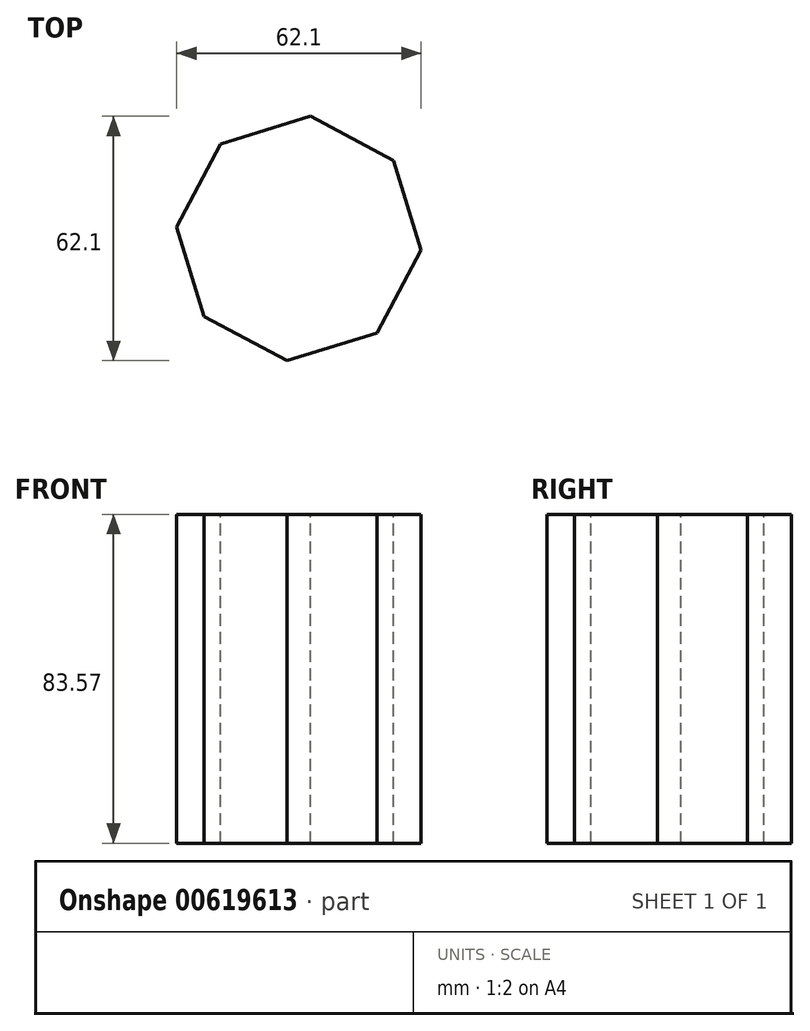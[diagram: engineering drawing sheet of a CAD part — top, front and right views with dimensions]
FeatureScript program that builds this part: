
annotation { "Feature Type Name" : "Feature", "Feature Type Description" : "" }
export const myFeature = defineFeature(function(context is Context, id is Id, definition is map)
    precondition{}
    {
        {
            var Q0;
            Q0=qCreatedBy(makeId("Top.planeOp"),FACE);
            var sketch = newSketch(context, id + "F0", { "sketchPlane" : qUnion([Q0])});
            skCircle(sketch, "E0.cCircle", {"center": v(0, 0) * mm, "radius": 28.82 * mm, "construction": true});
            skLineSegment(sketch, "E0.0", {"start": v(-19.86, 24.06) * mm, "end": v(2.97, 31.05) * mm});
            skLineSegment(sketch, "E0.1", {"start": v(2.97, 31.05) * mm, "end": v(24.06, 19.86) * mm});
            skLineSegment(sketch, "E0.2", {"start": v(24.06, 19.86) * mm, "end": v(31.05, -2.97) * mm});
            skLineSegment(sketch, "E0.3", {"start": v(31.05, -2.97) * mm, "end": v(19.86, -24.06) * mm});
            skLineSegment(sketch, "E0.4", {"start": v(19.86, -24.06) * mm, "end": v(-2.97, -31.05) * mm});
            skLineSegment(sketch, "E0.5", {"start": v(-2.97, -31.05) * mm, "end": v(-24.06, -19.86) * mm});
            skLineSegment(sketch, "E0.6", {"start": v(-24.06, -19.86) * mm, "end": v(-31.05, 2.97) * mm});
            skLineSegment(sketch, "E0.7", {"start": v(-31.05, 2.97) * mm, "end": v(-19.86, 24.06) * mm});
            skPoint(sketch, "E0.0.midPoint", {"position": v(-8.45, 27.56) * mm});
            skSolve(sketch);
        }
        {
            var Q0;
            Q0=makeQuery(id+"F0.imprint","IMPRINT",FACE,{"disambiguationData":[TD([[makeQuery(id+"F0.imprint","IMPRINT",EDGE,{"derivedFrom":sQuery(id+"F0.wireOp",EDGE,"E0.0")}),-1.0]])]});
            extrude(context, id + "F1", {"entities" : qUnion([Q0]), "oppositeDirection" : true, "depth" : 83.57 * mm, "offsetDistance" : 25.4 * mm});
        }
    });
